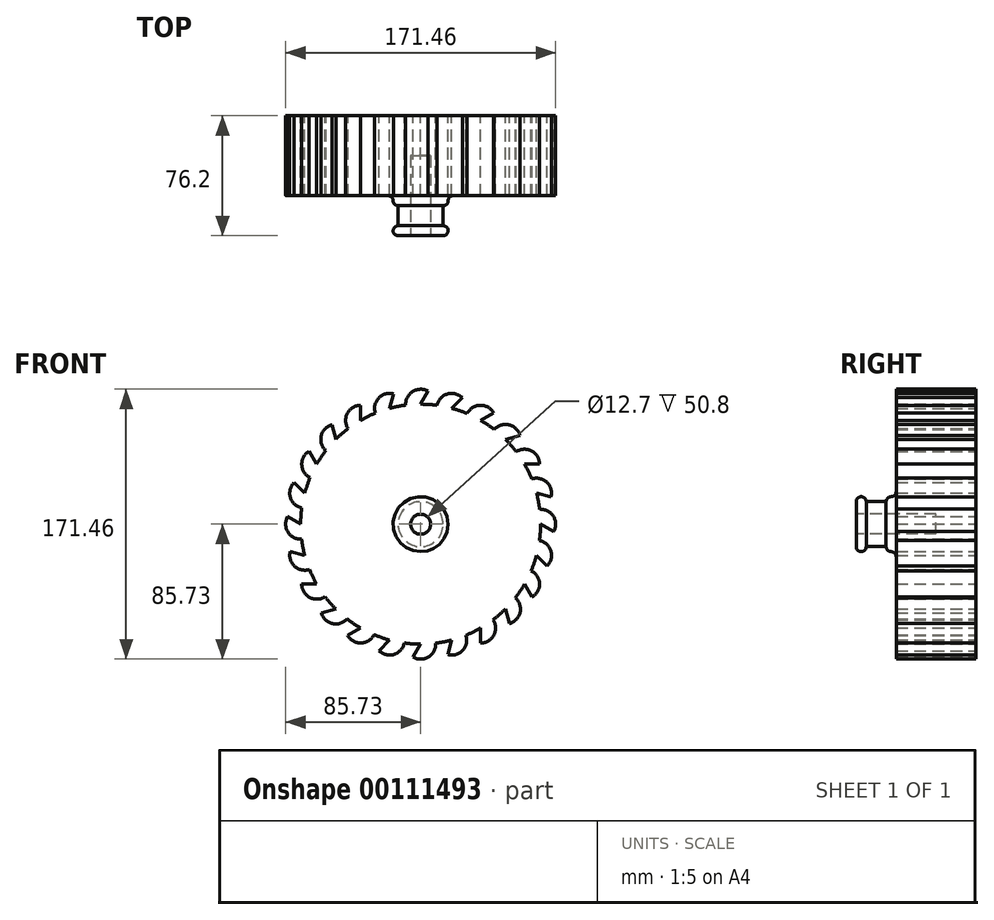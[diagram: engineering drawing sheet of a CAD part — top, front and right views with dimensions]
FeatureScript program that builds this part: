
annotation { "Feature Type Name" : "Feature", "Feature Type Description" : "" }
export const myFeature = defineFeature(function(context is Context, id is Id, definition is map)
    precondition{}
    {
        {
            var Q0;
            Q0=qCreatedBy(makeId("Front.planeOp"),FACE);
            var sketch = newSketch(context, id + "F0", { "sketchPlane" : qUnion([Q0])});
            skArc(sketch, "E0", {"start": v(-60.18, 46.74) * mm, "mid": v(-63.23, 42.52) * mm, "end": v(-66, 38.1) * mm});
            skArc(sketch, "E1", {"start": v(4.76, 84.45) * mm, "mid": v(-5.02, 84.3) * mm, "end": v(-9.5, 75.6) * mm});
            skLineSegment(sketch, "E2", {"start": v(0, 76.2) * mm, "end": v(4.76, 84.45) * mm});
            skLineSegment(sketch, "E3", {"start": v(0, 0) * mm, "end": v(46.66, 0) * mm, "construction": true});
            skArc(sketch, "E4.1.0", {"start": v(-17.26, 82.8) * mm, "mid": v(-26.66, 80.12) * mm, "end": v(-28.75, 70.57) * mm});
            skLineSegment(sketch, "E4.1.1", {"start": v(-19.72, 73.6) * mm, "end": v(-17.26, 82.8) * mm});
            skArc(sketch, "E4.2.0", {"start": v(-38.1, 75.52) * mm, "mid": v(-46.5, 70.5) * mm, "end": v(-46.04, 60.72) * mm});
            skLineSegment(sketch, "E4.2.1", {"start": v(-38.1, 66) * mm, "end": v(-38.1, 75.52) * mm});
            skArc(sketch, "E4.3.0", {"start": v(-56.35, 63.08) * mm, "mid": v(-63.15, 56.06) * mm, "end": v(-60.18, 46.74) * mm});
            skLineSegment(sketch, "E4.3.1", {"start": v(-53.88, 53.88) * mm, "end": v(-56.35, 63.08) * mm});
            skArc(sketch, "E4.4.0", {"start": v(-70.75, 46.35) * mm, "mid": v(-75.51, 37.8) * mm, "end": v(-70.23, 29.57) * mm});
            skLineSegment(sketch, "E4.4.1", {"start": v(-66, 38.1) * mm, "end": v(-70.75, 46.35) * mm});
            skArc(sketch, "E4.5.0", {"start": v(-80.34, 26.46) * mm, "mid": v(-82.72, 16.97) * mm, "end": v(-75.49, 10.39) * mm});
            skLineSegment(sketch, "E4.5.1", {"start": v(-73.6, 19.72) * mm, "end": v(-80.34, 26.46) * mm});
            skArc(sketch, "E4.6.0", {"start": v(-84.45, 4.76) * mm, "mid": v(-84.3, -5.02) * mm, "end": v(-75.6, -9.5) * mm});
            skLineSegment(sketch, "E4.6.1", {"start": v(-76.2, 0) * mm, "end": v(-84.45, 4.76) * mm});
            skArc(sketch, "E4.7.0", {"start": v(-82.8, -17.26) * mm, "mid": v(-80.12, -26.66) * mm, "end": v(-70.57, -28.75) * mm});
            skLineSegment(sketch, "E4.7.1", {"start": v(-73.6, -19.72) * mm, "end": v(-82.8, -17.26) * mm});
            skArc(sketch, "E4.8.0", {"start": v(-75.52, -38.1) * mm, "mid": v(-70.5, -46.5) * mm, "end": v(-60.72, -46.04) * mm});
            skLineSegment(sketch, "E4.8.1", {"start": v(-66, -38.1) * mm, "end": v(-75.52, -38.1) * mm});
            skArc(sketch, "E4.9.0", {"start": v(-63.08, -56.35) * mm, "mid": v(-56.06, -63.15) * mm, "end": v(-46.74, -60.18) * mm});
            skLineSegment(sketch, "E4.9.1", {"start": v(-53.88, -53.88) * mm, "end": v(-63.08, -56.35) * mm});
            skArc(sketch, "E4.10.0", {"start": v(-46.35, -70.75) * mm, "mid": v(-37.8, -75.51) * mm, "end": v(-29.57, -70.23) * mm});
            skLineSegment(sketch, "E4.10.1", {"start": v(-38.1, -66) * mm, "end": v(-46.35, -70.75) * mm});
            skArc(sketch, "E4.11.0", {"start": v(-26.46, -80.34) * mm, "mid": v(-16.97, -82.72) * mm, "end": v(-10.39, -75.49) * mm});
            skLineSegment(sketch, "E4.11.1", {"start": v(-19.72, -73.6) * mm, "end": v(-26.46, -80.34) * mm});
            skArc(sketch, "E4.12.0", {"start": v(-4.76, -84.45) * mm, "mid": v(5.02, -84.3) * mm, "end": v(9.5, -75.6) * mm});
            skLineSegment(sketch, "E4.12.1", {"start": v(0, -76.2) * mm, "end": v(-4.76, -84.45) * mm});
            skArc(sketch, "E4.13.0", {"start": v(17.26, -82.8) * mm, "mid": v(26.66, -80.12) * mm, "end": v(28.75, -70.57) * mm});
            skLineSegment(sketch, "E4.13.1", {"start": v(19.72, -73.6) * mm, "end": v(17.26, -82.8) * mm});
            skArc(sketch, "E4.14.0", {"start": v(38.1, -75.52) * mm, "mid": v(46.5, -70.5) * mm, "end": v(46.04, -60.72) * mm});
            skLineSegment(sketch, "E4.14.1", {"start": v(38.1, -66) * mm, "end": v(38.1, -75.52) * mm});
            skArc(sketch, "E4.15.0", {"start": v(56.35, -63.08) * mm, "mid": v(63.15, -56.06) * mm, "end": v(60.18, -46.74) * mm});
            skLineSegment(sketch, "E4.15.1", {"start": v(53.88, -53.88) * mm, "end": v(56.35, -63.08) * mm});
            skArc(sketch, "E4.16.0", {"start": v(70.75, -46.35) * mm, "mid": v(75.51, -37.8) * mm, "end": v(70.23, -29.57) * mm});
            skLineSegment(sketch, "E4.16.1", {"start": v(66, -38.1) * mm, "end": v(70.75, -46.35) * mm});
            skArc(sketch, "E4.17.0", {"start": v(80.34, -26.46) * mm, "mid": v(82.72, -16.97) * mm, "end": v(75.49, -10.39) * mm});
            skLineSegment(sketch, "E4.17.1", {"start": v(73.6, -19.72) * mm, "end": v(80.34, -26.46) * mm});
            skArc(sketch, "E4.18.0", {"start": v(84.45, -4.76) * mm, "mid": v(84.3, 5.02) * mm, "end": v(75.6, 9.5) * mm});
            skLineSegment(sketch, "E4.18.1", {"start": v(76.2, 0) * mm, "end": v(84.45, -4.76) * mm});
            skArc(sketch, "E4.19.0", {"start": v(82.8, 17.26) * mm, "mid": v(80.12, 26.66) * mm, "end": v(70.57, 28.75) * mm});
            skLineSegment(sketch, "E4.19.1", {"start": v(73.6, 19.72) * mm, "end": v(82.8, 17.26) * mm});
            skArc(sketch, "E4.20.0", {"start": v(75.52, 38.1) * mm, "mid": v(70.5, 46.5) * mm, "end": v(60.72, 46.04) * mm});
            skLineSegment(sketch, "E4.20.1", {"start": v(66, 38.1) * mm, "end": v(75.52, 38.1) * mm});
            skArc(sketch, "E4.21.0", {"start": v(63.08, 56.35) * mm, "mid": v(56.06, 63.15) * mm, "end": v(46.74, 60.18) * mm});
            skLineSegment(sketch, "E4.21.1", {"start": v(53.88, 53.88) * mm, "end": v(63.08, 56.35) * mm});
            skArc(sketch, "E4.22.0", {"start": v(46.35, 70.75) * mm, "mid": v(37.8, 75.51) * mm, "end": v(29.57, 70.23) * mm});
            skLineSegment(sketch, "E4.22.1", {"start": v(38.1, 66) * mm, "end": v(46.35, 70.75) * mm});
            skArc(sketch, "E4.23.0", {"start": v(26.46, 80.34) * mm, "mid": v(16.97, 82.72) * mm, "end": v(10.39, 75.49) * mm});
            skLineSegment(sketch, "E4.23.1", {"start": v(19.72, 73.6) * mm, "end": v(26.46, 80.34) * mm});
            skArc(sketch, "E5.trimOffspring", {"start": v(-70.23, 29.57) * mm, "mid": v(-72.08, 24.7) * mm, "end": v(-73.6, 19.72) * mm});
            skArc(sketch, "E6.trimOffspring", {"start": v(-46.04, 60.72) * mm, "mid": v(-50.08, 57.44) * mm, "end": v(-53.88, 53.88) * mm});
            skArc(sketch, "E7.trimOffspring", {"start": v(-75.49, 10.39) * mm, "mid": v(-76.02, 5.2) * mm, "end": v(-76.2, 0) * mm});
            skArc(sketch, "E8.trimOffspring", {"start": v(-75.6, -9.5) * mm, "mid": v(-74.78, -14.65) * mm, "end": v(-73.6, -19.72) * mm});
            skArc(sketch, "E9.trimOffspring", {"start": v(-70.57, -28.75) * mm, "mid": v(-68.44, -33.5) * mm, "end": v(-66, -38.1) * mm});
            skArc(sketch, "E10.trimOffspring", {"start": v(-60.72, -46.04) * mm, "mid": v(-57.44, -50.08) * mm, "end": v(-53.88, -53.88) * mm});
            skArc(sketch, "E11.trimOffspring", {"start": v(-46.74, -60.18) * mm, "mid": v(-42.52, -63.23) * mm, "end": v(-38.1, -66) * mm});
            skArc(sketch, "E12.trimOffspring", {"start": v(-29.57, -70.23) * mm, "mid": v(-24.7, -72.08) * mm, "end": v(-19.72, -73.6) * mm});
            skArc(sketch, "E13.trimOffspring", {"start": v(-10.39, -75.49) * mm, "mid": v(-5.2, -76.02) * mm, "end": v(0, -76.2) * mm});
            skArc(sketch, "E14.trimOffspring", {"start": v(9.5, -75.6) * mm, "mid": v(14.65, -74.78) * mm, "end": v(19.72, -73.6) * mm});
            skArc(sketch, "E15.trimOffspring", {"start": v(28.75, -70.57) * mm, "mid": v(33.5, -68.44) * mm, "end": v(38.1, -66) * mm});
            skArc(sketch, "E16.trimOffspring", {"start": v(46.04, -60.72) * mm, "mid": v(50.08, -57.44) * mm, "end": v(53.88, -53.88) * mm});
            skArc(sketch, "E17.trimOffspring", {"start": v(60.18, -46.74) * mm, "mid": v(63.23, -42.52) * mm, "end": v(66, -38.1) * mm});
            skArc(sketch, "E18.trimOffspring", {"start": v(70.23, -29.57) * mm, "mid": v(72.08, -24.7) * mm, "end": v(73.6, -19.72) * mm});
            skArc(sketch, "E19.trimOffspring", {"start": v(-28.75, 70.57) * mm, "mid": v(-33.5, 68.44) * mm, "end": v(-38.1, 66) * mm});
            skArc(sketch, "E20.trimOffspring", {"start": v(-9.5, 75.6) * mm, "mid": v(-14.65, 74.78) * mm, "end": v(-19.72, 73.6) * mm});
            skArc(sketch, "E21.trimOffspring", {"start": v(10.39, 75.49) * mm, "mid": v(5.2, 76.02) * mm, "end": v(0, 76.2) * mm});
            skArc(sketch, "E22.trimOffspring", {"start": v(29.57, 70.23) * mm, "mid": v(24.7, 72.08) * mm, "end": v(19.72, 73.6) * mm});
            skArc(sketch, "E23.trimOffspring", {"start": v(46.74, 60.18) * mm, "mid": v(42.52, 63.23) * mm, "end": v(38.1, 66) * mm});
            skArc(sketch, "E24.trimOffspring", {"start": v(60.72, 46.04) * mm, "mid": v(57.44, 50.08) * mm, "end": v(53.88, 53.88) * mm});
            skArc(sketch, "E25.trimOffspring", {"start": v(70.57, 28.75) * mm, "mid": v(68.44, 33.5) * mm, "end": v(66, 38.1) * mm});
            skArc(sketch, "E26.trimOffspring", {"start": v(75.6, 9.5) * mm, "mid": v(74.78, 14.65) * mm, "end": v(73.6, 19.72) * mm});
            skArc(sketch, "E27.trimOffspring", {"start": v(75.49, -10.39) * mm, "mid": v(76.02, -5.2) * mm, "end": v(76.2, 0) * mm});
            skSolve(sketch);
        }
        {
            var Q0;
            Q0 = qSketchRegion(id + "F0", true);
            extrude(context, id + "F1", {"entities" : qUnion([Q0]), "depth" : 50.8 * mm});
        }
        {
            var Q0;
            Q0=makeQuery(id+"F1.opExtrude","CAP_FACE",FACE,{"disambiguationData":[OSD([sQuery(id+"F0.wireOp",EDGE,"E0"),sQuery(id+"F0.wireOp",EDGE,"E1"),sQuery(id+"F0.wireOp",EDGE,"E2"),sQuery(id+"F0.wireOp",EDGE,"E4.1.0"),sQuery(id+"F0.wireOp",EDGE,"E4.1.1"),sQuery(id+"F0.wireOp",EDGE,"E4.2.0"),sQuery(id+"F0.wireOp",EDGE,"E4.2.1"),sQuery(id+"F0.wireOp",EDGE,"E4.3.0"),sQuery(id+"F0.wireOp",EDGE,"E4.3.1"),sQuery(id+"F0.wireOp",EDGE,"E4.4.0"),sQuery(id+"F0.wireOp",EDGE,"E4.4.1"),sQuery(id+"F0.wireOp",EDGE,"E4.5.0"),sQuery(id+"F0.wireOp",EDGE,"E4.5.1"),sQuery(id+"F0.wireOp",EDGE,"E4.6.0"),sQuery(id+"F0.wireOp",EDGE,"E4.6.1"),sQuery(id+"F0.wireOp",EDGE,"E4.7.0"),sQuery(id+"F0.wireOp",EDGE,"E4.7.1"),sQuery(id+"F0.wireOp",EDGE,"E4.8.0"),sQuery(id+"F0.wireOp",EDGE,"E4.8.1"),sQuery(id+"F0.wireOp",EDGE,"E4.9.0"),sQuery(id+"F0.wireOp",EDGE,"E4.9.1"),sQuery(id+"F0.wireOp",EDGE,"E4.10.0"),sQuery(id+"F0.wireOp",EDGE,"E4.10.1"),sQuery(id+"F0.wireOp",EDGE,"E4.11.0"),sQuery(id+"F0.wireOp",EDGE,"E4.11.1"),sQuery(id+"F0.wireOp",EDGE,"E4.12.0"),sQuery(id+"F0.wireOp",EDGE,"E4.12.1"),sQuery(id+"F0.wireOp",EDGE,"E4.13.0"),sQuery(id+"F0.wireOp",EDGE,"E4.13.1"),sQuery(id+"F0.wireOp",EDGE,"E4.14.0"),sQuery(id+"F0.wireOp",EDGE,"E4.14.1"),sQuery(id+"F0.wireOp",EDGE,"E4.15.0"),sQuery(id+"F0.wireOp",EDGE,"E4.15.1"),sQuery(id+"F0.wireOp",EDGE,"E4.16.0"),sQuery(id+"F0.wireOp",EDGE,"E4.16.1"),sQuery(id+"F0.wireOp",EDGE,"E4.17.0"),sQuery(id+"F0.wireOp",EDGE,"E4.17.1"),sQuery(id+"F0.wireOp",EDGE,"E4.18.0"),sQuery(id+"F0.wireOp",EDGE,"E4.18.1"),sQuery(id+"F0.wireOp",EDGE,"E4.19.0"),sQuery(id+"F0.wireOp",EDGE,"E4.19.1"),sQuery(id+"F0.wireOp",EDGE,"E4.20.0"),sQuery(id+"F0.wireOp",EDGE,"E4.20.1"),sQuery(id+"F0.wireOp",EDGE,"E4.21.0"),sQuery(id+"F0.wireOp",EDGE,"E4.21.1"),sQuery(id+"F0.wireOp",EDGE,"E4.22.0"),sQuery(id+"F0.wireOp",EDGE,"E4.22.1"),sQuery(id+"F0.wireOp",EDGE,"E4.23.0"),sQuery(id+"F0.wireOp",EDGE,"E4.23.1"),sQuery(id+"F0.wireOp",EDGE,"E5.trimOffspring"),sQuery(id+"F0.wireOp",EDGE,"E6.trimOffspring"),sQuery(id+"F0.wireOp",EDGE,"E7.trimOffspring"),sQuery(id+"F0.wireOp",EDGE,"E8.trimOffspring"),sQuery(id+"F0.wireOp",EDGE,"E9.trimOffspring"),sQuery(id+"F0.wireOp",EDGE,"E10.trimOffspring"),sQuery(id+"F0.wireOp",EDGE,"E11.trimOffspring"),sQuery(id+"F0.wireOp",EDGE,"E12.trimOffspring"),sQuery(id+"F0.wireOp",EDGE,"E13.trimOffspring"),sQuery(id+"F0.wireOp",EDGE,"E14.trimOffspring"),sQuery(id+"F0.wireOp",EDGE,"E15.trimOffspring"),sQuery(id+"F0.wireOp",EDGE,"E16.trimOffspring"),sQuery(id+"F0.wireOp",EDGE,"E17.trimOffspring"),sQuery(id+"F0.wireOp",EDGE,"E18.trimOffspring"),sQuery(id+"F0.wireOp",EDGE,"E19.trimOffspring"),sQuery(id+"F0.wireOp",EDGE,"E20.trimOffspring"),sQuery(id+"F0.wireOp",EDGE,"E21.trimOffspring"),sQuery(id+"F0.wireOp",EDGE,"E22.trimOffspring"),sQuery(id+"F0.wireOp",EDGE,"E23.trimOffspring"),sQuery(id+"F0.wireOp",EDGE,"E24.trimOffspring"),sQuery(id+"F0.wireOp",EDGE,"E25.trimOffspring"),sQuery(id+"F0.wireOp",EDGE,"E26.trimOffspring"),sQuery(id+"F0.wireOp",EDGE,"E27.trimOffspring")])],"isStart":false});
            var sketch = newSketch(context, id + "F2", { "sketchPlane" : qUnion([Q0])});
            skCircle(sketch, "E28", {"center": v(0, 0) * mm, "radius": 17.46 * mm});
            skSolve(sketch);
        }
        {
            var Q0;
            Q0 = qSketchRegion(id + "F2", true);
            extrude(context, id + "F3", {"entities" : qUnion([Q0]), "operationType" : NewBodyOperationType.ADD, "depth" : 6.35 * mm});
        }
        {
            var Q0;
            Q0=makeQuery(id+"F3.opExtrude","CAP_FACE",FACE,{"disambiguationData":[OSD([sQuery(id+"F2.wireOp",EDGE,"E28")])],"isStart":false});
            var sketch = newSketch(context, id + "F4", { "sketchPlane" : qUnion([Q0])});
            skCircle(sketch, "E29", {"center": v(0, 0) * mm, "radius": 14.29 * mm});
            skSolve(sketch);
        }
        {
            var Q0;
            Q0 = qSketchRegion(id + "F4", true);
            extrude(context, id + "F5", {"entities" : qUnion([Q0]), "operationType" : NewBodyOperationType.ADD, "depth" : 12.7 * mm});
        }
        {
            var Q0;
            Q0=makeQuery(id+"F5.opExtrude","CAP_FACE",FACE,{"disambiguationData":[OSD([sQuery(id+"F4.wireOp",EDGE,"E29")])],"isStart":false});
            var sketch = newSketch(context, id + "F6", { "sketchPlane" : qUnion([Q0])});
            skCircle(sketch, "E30", {"center": v(0, 0) * mm, "radius": 17.46 * mm});
            skSolve(sketch);
        }
        {
            var Q0;
            Q0 = qSketchRegion(id + "F6", true);
            extrude(context, id + "F7", {"entities" : qUnion([Q0]), "operationType" : NewBodyOperationType.ADD, "depth" : 6.35 * mm});
        }
        {
            var Q0;
            Q0=makeQuery(id+"F3.opExtrude","SWEPT_FACE",FACE,{"disambiguationData":[OSD([sQuery(id+"F2.wireOp",EDGE,"E28")])]});
            var Q1;
            Q1=makeQuery(id+"F7.opExtrude","SWEPT_FACE",FACE,{"disambiguationData":[OSD([sQuery(id+"F6.wireOp",EDGE,"E30")])]});
            fillet(context, id + "F8", {"entities" : qUnion([Q0, Q1]), "radius" : 3.17 * mm, "tangentPropagation" : true, "allowEdgeOverflow" : false});
        }
        {
            var Q0;
            Q0=makeQuery(id+"F7.opExtrude","CAP_FACE",FACE,{"disambiguationData":[OSD([sQuery(id+"F6.wireOp",EDGE,"E30")])],"isStart":false});
            var sketch = newSketch(context, id + "F9", { "sketchPlane" : qUnion([Q0])});
            skCircle(sketch, "E31", {"center": v(0, 0) * mm, "radius": 6.35 * mm});
            skSolve(sketch);
        }
        {
            var Q0;
            Q0 = qSketchRegion(id + "F9", true);
            extrude(context, id + "F10", {"entities" : qUnion([Q0]), "operationType" : NewBodyOperationType.REMOVE, "endBound" : BoundingType.THROUGH_ALL, "oppositeDirection" : true, "depth" : 25.4 * mm});
        }
        {
            var Q0;
            Q0 = qSketchRegion(id + "F0", true);
            extrude(context, id + "F11", {"entities" : qUnion([Q0]), "operationType" : NewBodyOperationType.ADD, "depth" : 25.4 * mm});
        }
    });
